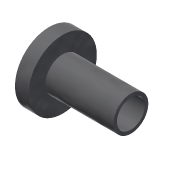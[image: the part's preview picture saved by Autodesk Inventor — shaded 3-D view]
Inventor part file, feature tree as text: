
AUTODESK INVENTOR PART (.ipt)
format: ipt  version: 2016 SP2 (Build 200236200, 236)  size: 102,912 bytes
history: native  units: mm
features: revolve x1, sketch x1
ambient origin geometry x8: Origin, YZ Plane, XZ Plane, XY Plane, X Axis, Y Axis, Z Axis, Center Point
bodies: Solid1 (feature_tree)
feature tree (2):
  revolve  "Revolution1"  [1 undecoded]
  sketch  "Sketch1"  dims[d0=5.0mm d1=2.05mm d2=2.55mm d3=12.0mm d4=10.0mm d5=90.0deg]
note: 1 required parameter value undecoded (feature->parameter linkage not recoverable at this tier; creation-order binding heuristic only, values carry confidence <= 0.55)
